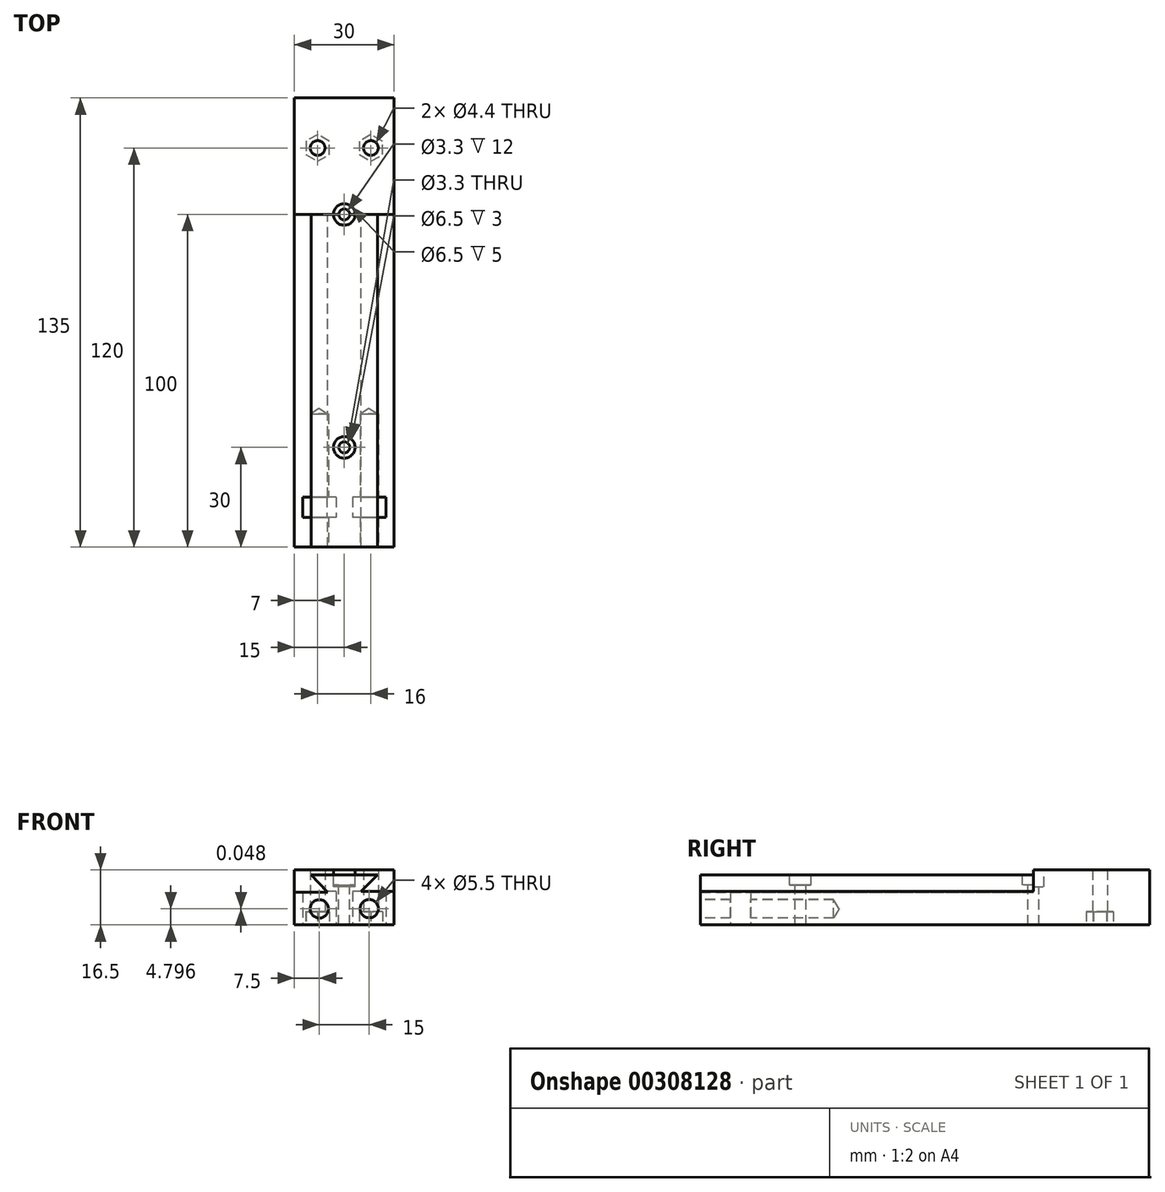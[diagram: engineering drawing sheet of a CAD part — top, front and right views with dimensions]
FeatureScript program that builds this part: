
annotation { "Feature Type Name" : "Feature", "Feature Type Description" : "" }
export const myFeature = defineFeature(function(context is Context, id is Id, definition is map)
    precondition{}
    {
        {
            var Q0;
            Q0=qCreatedBy(makeId("Front.planeOp"),FACE);
            var sketch = newSketch(context, id + "F0", { "sketchPlane" : qUnion([Q0])});
            skPoint(sketch, "E0.0", {"position": v(-39.87, -5.55) * mm});
            skPoint(sketch, "E1.0", {"position": v(-9.87, 4.45) * mm});
            skPoint(sketch, "E2.0", {"position": v(-34.54, 0.5) * mm});
            skPoint(sketch, "E3.0", {"position": v(-33.62, -2.92) * mm});
            skPoint(sketch, "E4.0", {"position": v(-29.87, -0.75) * mm});
            skPoint(sketch, "E5.0", {"position": v(-19.54, -1.96) * mm});
            skPoint(sketch, "E6.0", {"position": v(-15.6, 1.06) * mm});
            skPoint(sketch, "E7.0", {"position": v(-15.2, -1.96) * mm});
            skCircle(sketch, "E8", {"center": v(-32.37, -0.75) * mm, "radius": 2.5 * mm});
            skCircle(sketch, "E9", {"center": v(-17.37, -0.7) * mm, "radius": 2.5 * mm});
            skLineSegment(sketch, "E10.bottom", {"start": v(-39.87, -5.55) * mm, "end": v(-39.87, 4.25) * mm});
            skLineSegment(sketch, "E10.top", {"start": v(-9.87, -5.55) * mm, "end": v(-9.87, 4.45) * mm});
            skLineSegment(sketch, "E10.left", {"start": v(-39.87, -5.55) * mm, "end": v(-9.87, -5.55) * mm});
            skLineSegment(sketch, "E11", {"start": v(-39.87, 4.25) * mm, "end": v(-29.87, 4.25) * mm});
            skLineSegment(sketch, "E12", {"start": v(-9.87, 4.45) * mm, "end": v(-19.87, 4.45) * mm});
            skLineSegment(sketch, "E13", {"start": v(-29.87, 4.25) * mm, "end": v(-34.87, 9.45) * mm});
            skLineSegment(sketch, "E14", {"start": v(-19.87, 4.45) * mm, "end": v(-14.87, 9.45) * mm});
            skLineSegment(sketch, "E15", {"start": v(-34.87, 9.45) * mm, "end": v(-24.87, 9.45) * mm});
            skPoint(sketch, "E16.endSnap0", {"position": v(-24.87, 9.45) * mm});
            skLineSegment(sketch, "E17", {"start": v(-24.87, 9.45) * mm, "end": v(-14.87, 9.45) * mm});
            skSolve(sketch);
        }
        {
            var Q0;
            Q0=makeQuery(id+"F0.imprint","IMPRINT",FACE,{"disambiguationData":[TD([[makeQuery(id+"F0.imprint","IMPRINT",EDGE,{"derivedFrom":sQuery(id+"F0.wireOp",EDGE,"E8")}),-1.0]])]});
            var Q1;
            {var subQ0=sQuery(id+"F0.wireOp",EDGE,"716d0718-7f4a-4372-b67f-45226a862b40.bottom");Q1=makeQuery(id+"F0.imprint","IMPRINT",FACE,{"disambiguationData":[TD([[makeQuery(id+"F0.imprint","IMPRINT",EDGE,{"derivedFrom":subQ0}),1.0]])]});}
            var Q2;
            {var subQ2=sQuery(id+"F0.wireOp",EDGE,"ff0e58af-8eab-48c5-9db7-a835ad51614d.bottom");Q2=makeQuery(id+"F0.imprint","IMPRINT",FACE,{"disambiguationData":[TD([[makeQuery(id+"F0.imprint","IMPRINT",EDGE,{"derivedFrom":subQ2}),1.0]])]});}
            var Q3;
            Q3=makeQuery(id+"F0.imprint","IMPRINT",FACE,{"disambiguationData":[TD([[makeQuery(id+"F0.imprint","IMPRINT",EDGE,{"derivedFrom":sQuery(id+"F0.wireOp",EDGE,"E8")}),1.0]])]});
            var Q4;
            Q4=makeQuery(id+"F0.imprint","IMPRINT",FACE,{"disambiguationData":[TD([[makeQuery(id+"F0.imprint","IMPRINT",EDGE,{"derivedFrom":sQuery(id+"F0.wireOp",EDGE,"E9")}),1.0]])]});
            var Q5;
            Q5=makeQuery(id+"F0.imprint","IMPRINT",FACE,{"disambiguationData":[TD([[makeQuery(id+"F0.imprint","IMPRINT",EDGE,{"derivedFrom":sQuery(id+"F0.wireOp",EDGE,"716d0718-7f4a-4372-b67f-45226a862b40.left")}),1.0]])]});
            extrude(context, id + "F1", {"entities" : qUnion([Q0, Q1, Q2, Q3, Q4, Q5]), "depth" : 100 * mm});
        }
        {
            var Q0;
            Q0=makeQuery(id+"F1.opExtrude","CAP_FACE",FACE,{"disambiguationData":[OSD([sQuery(id+"F0.wireOp",EDGE,"E8"),sQuery(id+"F0.wireOp",EDGE,"E9"),sQuery(id+"F0.wireOp",EDGE,"E10.bottom"),sQuery(id+"F0.wireOp",EDGE,"E10.top"),sQuery(id+"F0.wireOp",EDGE,"E10.left"),sQuery(id+"F0.wireOp",EDGE,"E10.right"),sQuery(id+"F0.wireOp",EDGE,"716d0718-7f4a-4372-b67f-45226a862b40.bottom"),sQuery(id+"F0.wireOp",EDGE,"716d0718-7f4a-4372-b67f-45226a862b40.top"),sQuery(id+"F0.wireOp",EDGE,"ff0e58af-8eab-48c5-9db7-a835ad51614d.bottom"),sQuery(id+"F0.wireOp",EDGE,"ff0e58af-8eab-48c5-9db7-a835ad51614d.top"),sQuery(id+"F0.wireOp",EDGE,"ff0e58af-8eab-48c5-9db7-a835ad51614d.left"),sQuery(id+"F0.wireOp",EDGE,"ff0e58af-8eab-48c5-9db7-a835ad51614d.right")])],"isStart":true});
            var sketch = newSketch(context, id + "F2", { "sketchPlane" : qUnion([Q0])});
            skLineSegment(sketch, "E18.bottom", {"start": v(9.87, -5.55) * mm, "end": v(39.87, -5.55) * mm});
            skLineSegment(sketch, "E18.top", {"start": v(9.87, 10.95) * mm, "end": v(39.87, 10.95) * mm});
            skLineSegment(sketch, "E18.left", {"start": v(9.87, -5.55) * mm, "end": v(9.87, 10.95) * mm});
            skLineSegment(sketch, "E18.right", {"start": v(39.87, -5.55) * mm, "end": v(39.87, 10.95) * mm});
            skSolve(sketch);
        }
        {
            var Q0;
            {var subQ0=sQuery(id+"F0.wireOp",EDGE,"716d0718-7f4a-4372-b67f-45226a862b40.top");Q0=makeQuery(id+"F2.imprint","IMPRINT",FACE,{"disambiguationData":[TD([[makeQuery(id+"F2.imprint","IMPRINT",EDGE,{"derivedFrom":makeQuery(id+"F1.opExtrude","CAP_EDGE",EDGE,{"disambiguationData":[OSD([subQ0])],"isStart":true})}),-1.0]])]});}
            var Q1;
            {var subQ1=sQuery(id+"F0.wireOp",EDGE,"716d0718-7f4a-4372-b67f-45226a862b40.bottom");Q1=makeQuery(id+"F2.imprint","IMPRINT",FACE,{"disambiguationData":[TD([[makeQuery(id+"F2.imprint","IMPRINT",EDGE,{"derivedFrom":makeQuery(id+"F1.opExtrude","CAP_EDGE",EDGE,{"disambiguationData":[OSD([subQ1])],"isStart":true})}),1.0]])]});}
            var Q2;
            Q2=makeQuery(id+"F2.imprint","IMPRINT",FACE,{"disambiguationData":[TD([[makeQuery(id+"F2.imprint","IMPRINT",EDGE,{"derivedFrom":makeQuery(id+"F1.opExtrude","CAP_EDGE",EDGE,{"disambiguationData":[OSD([sQuery(id+"F0.wireOp",EDGE,"E8")])],"isStart":true})}),-1.0]])]});
            var Q3;
            Q3=makeQuery(id+"F2.imprint","IMPRINT",FACE,{"disambiguationData":[TD([[makeQuery(id+"F2.imprint","IMPRINT",EDGE,{"derivedFrom":makeQuery(id+"F1.opExtrude","CAP_EDGE",EDGE,{"disambiguationData":[OSD([sQuery(id+"F0.wireOp",EDGE,"E9")])],"isStart":true})}),-1.0]])]});
            var Q4;
            {var subQ6=sQuery(id+"F2.wireOp",EDGE,"E18.bottom");Q4=makeQuery(id+"F2.imprint","IMPRINT",FACE,{"disambiguationData":[TD([[makeQuery(id+"F2.imprint","IMPRINT",EDGE,{"derivedFrom":subQ6}),-1.0]])]});}
            var Q5;
            {var subQ2=sQuery(id+"F2.wireOp",EDGE,"E18.top");Q5=makeQuery(id+"F2.imprint","IMPRINT",FACE,{"disambiguationData":[TD([[makeQuery(id+"F2.imprint","IMPRINT",EDGE,{"derivedFrom":subQ2}),-1.0]])]});}
            extrude(context, id + "F3", {"entities" : qUnion([Q0, Q1, Q2, Q3, Q4, Q5]), "depth" : 35 * mm});
        }
        {
            var Q0;
            Q0=makeQuery(id+"F3.opExtrude","SWEPT_BODY",BODY,{"disambiguationData":[OSD([sQuery(id+"F2.wireOp",EDGE,"E18.bottom"),sQuery(id+"F2.wireOp",EDGE,"E18.top"),sQuery(id+"F2.wireOp",EDGE,"E18.left"),sQuery(id+"F2.wireOp",EDGE,"E18.right")])]});
            var Q1;
            Q1=makeQuery(id+"F1.opExtrude","SWEPT_BODY",BODY,{"disambiguationData":[OSD([sQuery(id+"F0.wireOp",EDGE,"E8"),sQuery(id+"F0.wireOp",EDGE,"E9"),sQuery(id+"F0.wireOp",EDGE,"E10.bottom"),sQuery(id+"F0.wireOp",EDGE,"E10.top"),sQuery(id+"F0.wireOp",EDGE,"E10.left"),sQuery(id+"F0.wireOp",EDGE,"E10.right"),sQuery(id+"F0.wireOp",EDGE,"716d0718-7f4a-4372-b67f-45226a862b40.bottom"),sQuery(id+"F0.wireOp",EDGE,"716d0718-7f4a-4372-b67f-45226a862b40.top"),sQuery(id+"F0.wireOp",EDGE,"ff0e58af-8eab-48c5-9db7-a835ad51614d.bottom"),sQuery(id+"F0.wireOp",EDGE,"ff0e58af-8eab-48c5-9db7-a835ad51614d.top"),sQuery(id+"F0.wireOp",EDGE,"ff0e58af-8eab-48c5-9db7-a835ad51614d.left"),sQuery(id+"F0.wireOp",EDGE,"ff0e58af-8eab-48c5-9db7-a835ad51614d.right")])]});
            booleanBodies(context, id + "F4", {"operationType" : BooleanOperationType.UNION, "tools" : qUnion([Q0, Q1])});
        }
        {
            var Q0;
            Q0=makeQuery(id+"F4.opBoolean","MERGE",FACE,{"derivedFrom":[makeQuery(id+"F1.opExtrude","SWEPT_FACE",FACE,{"disambiguationData":[OSD([sQuery(id+"F0.wireOp",EDGE,"E10.left")])]}),makeQuery(id+"F3.opExtrude","SWEPT_FACE",FACE,{"disambiguationData":[OSD([sQuery(id+"F2.wireOp",EDGE,"E18.bottom")])]})]});
            var sketch = newSketch(context, id + "F5", { "sketchPlane" : qUnion([Q0])});
            skPoint(sketch, "E19", {"position": v(-16.87, -20) * mm});
            skPoint(sketch, "E20", {"position": v(-32.87, -20) * mm});
            skLineSegment(sketch, "E21.bottom", {"start": v(-12.37, 85) * mm, "end": v(-22.37, 85) * mm});
            skLineSegment(sketch, "E21.top", {"start": v(-12.37, 91) * mm, "end": v(-22.37, 91) * mm});
            skLineSegment(sketch, "E21.left", {"start": v(-12.37, 85) * mm, "end": v(-12.37, 91) * mm});
            skLineSegment(sketch, "E21.right", {"start": v(-22.37, 85) * mm, "end": v(-22.37, 91) * mm});
            skLineSegment(sketch, "E22.bottom", {"start": v(-27.37, 85) * mm, "end": v(-37.37, 85) * mm});
            skLineSegment(sketch, "E22.top", {"start": v(-27.37, 91) * mm, "end": v(-37.37, 91) * mm});
            skLineSegment(sketch, "E22.left", {"start": v(-27.37, 85) * mm, "end": v(-27.37, 91) * mm});
            skLineSegment(sketch, "E22.right", {"start": v(-37.37, 85) * mm, "end": v(-37.37, 91) * mm});
            skCircle(sketch, "E23.cCircle", {"center": v(-16.87, -20) * mm, "radius": 3.5 * mm, "construction": true});
            skLineSegment(sketch, "E23.0", {"start": v(-20.37, -22.02) * mm, "end": v(-20.37, -17.98) * mm});
            skLineSegment(sketch, "E23.1", {"start": v(-20.37, -17.98) * mm, "end": v(-16.87, -15.96) * mm});
            skLineSegment(sketch, "E23.2", {"start": v(-16.87, -15.96) * mm, "end": v(-13.37, -17.98) * mm});
            skLineSegment(sketch, "E23.3", {"start": v(-13.37, -17.98) * mm, "end": v(-13.37, -22.02) * mm});
            skLineSegment(sketch, "E23.4", {"start": v(-13.37, -22.02) * mm, "end": v(-16.87, -24.04) * mm});
            skLineSegment(sketch, "E23.5", {"start": v(-16.87, -24.04) * mm, "end": v(-20.37, -22.02) * mm});
            skPoint(sketch, "E23.0.midPoint", {"position": v(-20.37, -20) * mm});
            skCircle(sketch, "E24.cCircle", {"center": v(-32.87, -20) * mm, "radius": 3.5 * mm, "construction": true});
            skLineSegment(sketch, "E24.0", {"start": v(-29.33, -21.96) * mm, "end": v(-32.8, -24.04) * mm});
            skLineSegment(sketch, "E24.1", {"start": v(-32.8, -24.04) * mm, "end": v(-36.33, -22.08) * mm});
            skLineSegment(sketch, "E24.2", {"start": v(-36.33, -22.08) * mm, "end": v(-36.4, -18.04) * mm});
            skLineSegment(sketch, "E24.3", {"start": v(-36.4, -18.04) * mm, "end": v(-32.94, -15.96) * mm});
            skLineSegment(sketch, "E24.4", {"start": v(-32.94, -15.96) * mm, "end": v(-29.4, -17.92) * mm});
            skLineSegment(sketch, "E24.5", {"start": v(-29.4, -17.92) * mm, "end": v(-29.33, -21.96) * mm});
            skPoint(sketch, "E24.0.midPoint", {"position": v(-31.07, -23) * mm});
            skSolve(sketch);
        }
        {
            var Q0;
            Q0=sQuery(id+"F5.wireOp",VERTEX,"E19");
            var Q1;
            Q1=sQuery(id+"F5.wireOp",VERTEX,"E20");
            var Q2;
            Q2=makeQuery(id+"F3.opExtrude","SWEPT_BODY",BODY,{"disambiguationData":[OSD([sQuery(id+"F2.wireOp",EDGE,"E18.bottom"),sQuery(id+"F2.wireOp",EDGE,"E18.top"),sQuery(id+"F2.wireOp",EDGE,"E18.left"),sQuery(id+"F2.wireOp",EDGE,"E18.right")])]});
            hole(context, id + "F6", {"style" : HoleStyle.SIMPLE, "endStyle" : HoleEndStyle.BLIND, "standardTappedOrClearance" : lookupTablePath({ "standard" : "ISO", "fit" : "Normal", "size" : "M4", "type" : "Clearance" }), "standardBlindInLast" : lookupTablePath({ "fit" : "Standard", "standard" : "ISO", "size" : "M4", "type" : "Clearance" }), "holeDiameter" : 4.4 * mm, "holeDepth" : 40 * mm, "isTappedThrough" : true, "tappedDepth" : 12 * mm, "tapClearance" : 3, "locations" : qUnion([Q0, Q1]), "scope" : qUnion([Q2])});
        }
        {
            var Q0;
            Q0=makeQuery(id+"F5.imprint","IMPRINT",FACE,{"disambiguationData":[TD([[makeQuery(id+"F5.imprint","IMPRINT",EDGE,{"derivedFrom":sQuery(id+"F5.wireOp",EDGE,"E21.bottom")}),-1.0]])]});
            var Q1;
            Q1=makeQuery(id+"F5.imprint","IMPRINT",FACE,{"disambiguationData":[TD([[makeQuery(id+"F5.imprint","IMPRINT",EDGE,{"derivedFrom":sQuery(id+"F5.wireOp",EDGE,"E22.bottom")}),-1.0]])]});
            extrude(context, id + "F7", {"entities" : qUnion([Q0, Q1]), "operationType" : NewBodyOperationType.REMOVE, "oppositeDirection" : true, "depth" : 10 * mm});
        }
        {
            var Q0;
            Q0=makeQuery(id+"F1.opExtrude","CAP_FACE",FACE,{"disambiguationData":[OSD([sQuery(id+"F0.wireOp",EDGE,"E10.bottom"),sQuery(id+"F0.wireOp",EDGE,"E10.top"),sQuery(id+"F0.wireOp",EDGE,"E10.left"),sQuery(id+"F0.wireOp",EDGE,"E10.right"),sQuery(id+"F0.wireOp",EDGE,"716d0718-7f4a-4372-b67f-45226a862b40.bottom"),sQuery(id+"F0.wireOp",EDGE,"716d0718-7f4a-4372-b67f-45226a862b40.top"),sQuery(id+"F0.wireOp",EDGE,"ff0e58af-8eab-48c5-9db7-a835ad51614d.bottom"),sQuery(id+"F0.wireOp",EDGE,"ff0e58af-8eab-48c5-9db7-a835ad51614d.top"),sQuery(id+"F0.wireOp",EDGE,"ff0e58af-8eab-48c5-9db7-a835ad51614d.left"),sQuery(id+"F0.wireOp",EDGE,"ff0e58af-8eab-48c5-9db7-a835ad51614d.right")])],"isStart":false});
            var sketch = newSketch(context, id + "F8", { "sketchPlane" : qUnion([Q0])});
            skPoint(sketch, "E25.0", {"position": v(-32.37, -0.75) * mm});
            skPoint(sketch, "E26.0", {"position": v(-17.37, -0.7) * mm});
            skSolve(sketch);
        }
        {
            var Q0;
            Q0=sQuery(id+"F8.wireOp",VERTEX,"E25.0");
            var Q1;
            Q1=sQuery(id+"F8.wireOp",VERTEX,"E26.0");
            var Q2;
            Q2=makeQuery(id+"F3.opExtrude","SWEPT_BODY",BODY,{"disambiguationData":[OSD([sQuery(id+"F2.wireOp",EDGE,"E18.bottom"),sQuery(id+"F2.wireOp",EDGE,"E18.top"),sQuery(id+"F2.wireOp",EDGE,"E18.left"),sQuery(id+"F2.wireOp",EDGE,"E18.right")])]});
            hole(context, id + "F9", {"style" : HoleStyle.SIMPLE, "endStyle" : HoleEndStyle.BLIND, "standardTappedOrClearance" : lookupTablePath({ "standard" : "ISO", "fit" : "Normal", "size" : "M5", "type" : "Clearance" }), "standardBlindInLast" : lookupTablePath({ "fit" : "Standard", "standard" : "ISO", "size" : "M5", "type" : "Clearance" }), "holeDiameter" : 5.5 * mm, "holeDepth" : 40 * mm, "isTappedThrough" : true, "tappedDepth" : 12 * mm, "tapClearance" : 3, "locations" : qUnion([Q0, Q1]), "scope" : qUnion([Q2])});
        }
        {
            var Q0;
            Q0=makeQuery(id+"F5.imprint","IMPRINT",FACE,{"disambiguationData":[TD([[makeQuery(id+"F5.imprint","IMPRINT",EDGE,{"derivedFrom":sQuery(id+"F5.wireOp",EDGE,"E23.0")}),-1.0]])]});
            var Q1;
            Q1=makeQuery(id+"F5.imprint","IMPRINT",FACE,{"disambiguationData":[TD([[makeQuery(id+"F5.imprint","IMPRINT",EDGE,{"derivedFrom":sQuery(id+"F5.wireOp",EDGE,"E24.0")}),-1.0]])]});
            extrude(context, id + "F10", {"entities" : qUnion([Q0, Q1]), "operationType" : NewBodyOperationType.REMOVE, "oppositeDirection" : true, "depth" : 4 * mm});
        }
        {
            var Q0;
            Q0=makeQuery(id+"F1.opExtrude","SWEPT_FACE",FACE,{"disambiguationData":[OSD([sQuery(id+"F0.wireOp",EDGE,"E15")])]});
            var sketch = newSketch(context, id + "F11", { "sketchPlane" : qUnion([Q0])});
            skLineSegment(sketch, "E27", {"start": v(-24.87, -100) * mm, "end": v(-24.87, 0) * mm, "construction": true});
            skPoint(sketch, "E28", {"position": v(-24.87, 0) * mm});
            skPoint(sketch, "E29", {"position": v(-24.87, -70) * mm});
            skSolve(sketch);
        }
        {
            var Q0;
            Q0=sQuery(id+"F11.wireOp",VERTEX,"E28");
            var Q1;
            Q1=sQuery(id+"F11.wireOp",VERTEX,"E29");
            var Q2;
            Q2=makeQuery(id+"F3.opExtrude","SWEPT_BODY",BODY,{"disambiguationData":[OSD([sQuery(id+"F2.wireOp",EDGE,"E18.bottom"),sQuery(id+"F2.wireOp",EDGE,"E18.top"),sQuery(id+"F2.wireOp",EDGE,"E18.left"),sQuery(id+"F2.wireOp",EDGE,"E18.right")])]});
            hole(context, id + "F12", {"style" : HoleStyle.C_BORE, "endStyle" : HoleEndStyle.THROUGH, "standardTappedOrClearance" : lookupTablePath({ "standard" : "ISO", "fit" : "Normal", "size" : "M3", "type" : "Clearance" }), "standardBlindInLast" : lookupTablePath({ "fit" : "Standard", "standard" : "ISO", "size" : "M3", "type" : "Clearance" }), "holeDiameter" : 3.3 * mm, "cBoreDiameter" : 6.5 * mm, "cBoreDepth" : 3 * mm, "isTappedThrough" : true, "tappedDepth" : 12 * mm, "tapClearance" : 3, "locations" : qUnion([Q0, Q1]), "scope" : qUnion([Q2])});
        }
        {
            var Q0;
            Q0=makeQuery(id+"F3.opExtrude","SWEPT_FACE",FACE,{"disambiguationData":[OSD([sQuery(id+"F2.wireOp",EDGE,"E18.top")])]});
            var sketch = newSketch(context, id + "F13", { "sketchPlane" : qUnion([Q0])});
            skCircle(sketch, "E30", {"center": v(-24.87, 0) * mm, "radius": 3.25 * mm});
            skSolve(sketch);
        }
        {
            var Q0;
            {var subQ0=sQuery(id+"F13.wireOp",EDGE,"E30");var subQ1=makeQuery(id+"F3.opExtrude","CAP_EDGE",EDGE,{"disambiguationData":[OSD([sQuery(id+"F2.wireOp",EDGE,"E18.top")])],"isStart":true});var subQ2=makeQuery(id+"F13.imprint","INTERSECT",VERTEX,{"disambiguationData":[OD(0.0)],"derivedFrom":[subQ1,subQ0]});Q0=makeQuery(id+"F13.imprint","IMPRINT",FACE,{"disambiguationData":[TD([[makeQuery(id+"F13.imprint","IMPRINT",EDGE,{"disambiguationData":[TD([[subQ2,-1.0]])],"derivedFrom":subQ0}),1.0]])]});}
            extrude(context, id + "F14", {"entities" : qUnion([Q0]), "operationType" : NewBodyOperationType.REMOVE, "oppositeDirection" : true, "depth" : 5 * mm});
        }
    });
